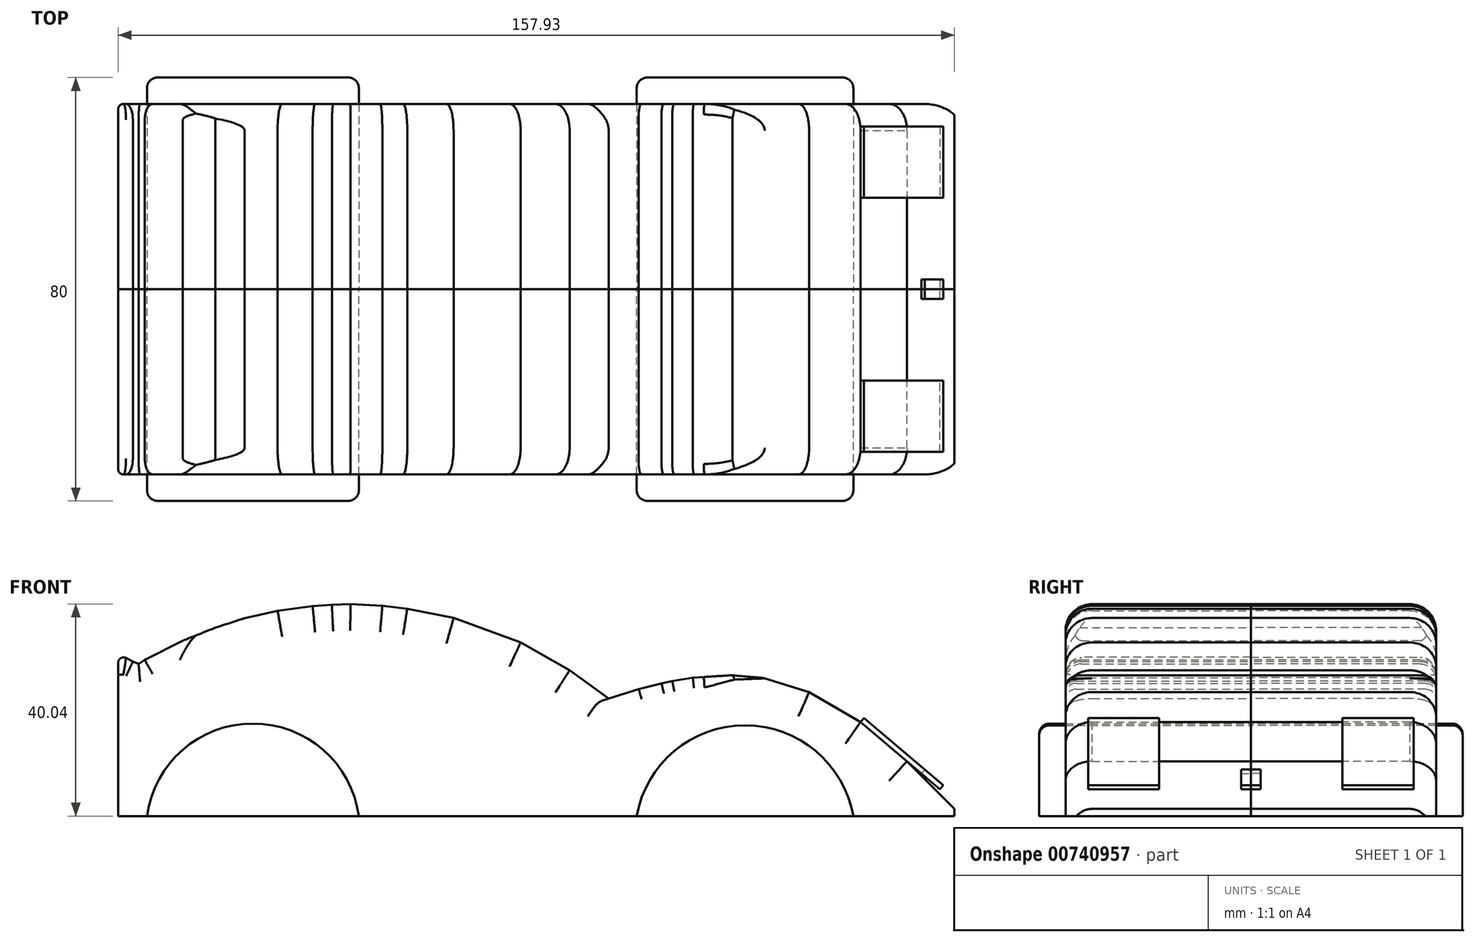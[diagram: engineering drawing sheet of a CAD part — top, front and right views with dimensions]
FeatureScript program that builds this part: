
annotation { "Feature Type Name" : "Feature", "Feature Type Description" : "" }
export const myFeature = defineFeature(function(context is Context, id is Id, definition is map)
    precondition{}
    {
        {
            var Q0;
            Q0=qCreatedBy(makeId("Front.planeOp"),FACE);
            var sketch = newSketch(context, id + "F0", { "sketchPlane" : qUnion([Q0])});
            skPoint(sketch, "E0.bottom.start.orphan", {"position": v(-35.35, 0) * mm});
            skLineSegment(sketch, "E1", {"start": v(-55.67, 30.52) * mm, "end": v(-53.12, 29.19) * mm});
            skPoint(sketch, "E2.startSnap0", {"position": v(70.97, 10.7) * mm});
            skPoint(sketch, "E3.orphan", {"position": v(70.97, 21.41) * mm});
            skPoint(sketch, "E4.orphan", {"position": v(-53.08, 6.08) * mm});
            skPoint(sketch, "E5.bottom.start.orphan", {"position": v(-55.9, 0) * mm});
            skPoint(sketch, "E6.orphan", {"position": v(-18.13, 0) * mm});
            skPoint(sketch, "E7.trimOffspring.end.orphan", {"position": v(70.97, 0) * mm});
            skPoint(sketch, "E8.orphan", {"position": v(86.43, 0) * mm});
            skPoint(sketch, "E9.orphan", {"position": v(86.43, 0.74) * mm});
            skPoint(sketch, "E10.0.internal.orphan", {"position": v(86.43, 10.7) * mm});
            skPoint(sketch, "E10.1.internal.orphan", {"position": v(102.02, 1.35) * mm});
            skLineSegment(sketch, "E11", {"start": v(102.02, 0) * mm, "end": v(102.02, 1.35) * mm});
            skLineSegment(sketch, "E12", {"start": v(102.02, 0) * mm, "end": v(-55.9, 0) * mm});
            skPoint(sketch, "E13.trimOffspring.end.orphan", {"position": v(-18.13, 6.08) * mm});
            skPoint(sketch, "E14.orphan", {"position": v(-18.13, 1.35) * mm});
            skPoint(sketch, "E15.start.orphan", {"position": v(86.43, 1.35) * mm});
            skArc(sketch, "E16", {"start": v(-10.44, 0) * mm, "mid": v(-30.45, 17.47) * mm, "end": v(-50.46, 0) * mm});
            skArc(sketch, "E17", {"start": v(82.95, 0) * mm, "mid": v(62.5, 17.15) * mm, "end": v(42.03, 0) * mm});
            skLineSegment(sketch, "E18", {"start": v(-55.88, 30.45) * mm, "end": v(-55.88, 30.6) * mm});
            skLineSegment(sketch, "E19", {"start": v(-55.88, 30.6) * mm, "end": v(-55.87, 30.6) * mm});
            skLineSegment(sketch, "E20", {"start": v(-55.87, 30.6) * mm, "end": v(-55.87, 30.6) * mm});
            skLineSegment(sketch, "E21", {"start": v(-55.87, 30.6) * mm, "end": v(-55.83, 30.58) * mm});
            skLineSegment(sketch, "E22", {"start": v(-55.83, 30.58) * mm, "end": v(-55.67, 30.52) * mm});
            skLineSegment(sketch, "E23", {"start": v(-53.12, 29.19) * mm, "end": v(-52.04, 28.74) * mm});
            skLineSegment(sketch, "E24", {"start": v(-52.04, 28.74) * mm, "end": v(-50.87, 29.48) * mm});
            skLineSegment(sketch, "E25", {"start": v(-50.87, 29.48) * mm, "end": v(-43.68, 33.14) * mm});
            skLineSegment(sketch, "E26", {"start": v(-43.68, 33.14) * mm, "end": v(-37.53, 35.58) * mm});
            skLineSegment(sketch, "E27", {"start": v(-37.53, 35.58) * mm, "end": v(-32, 37.39) * mm});
            skLineSegment(sketch, "E28", {"start": v(-32, 37.39) * mm, "end": v(-25.8, 38.8) * mm});
            skLineSegment(sketch, "E29", {"start": v(-25.8, 38.8) * mm, "end": v(-19.17, 39.68) * mm});
            skLineSegment(sketch, "E30", {"start": v(-19.17, 39.68) * mm, "end": v(-15.54, 39.9) * mm});
            skLineSegment(sketch, "E31", {"start": v(-15.54, 39.9) * mm, "end": v(-12.03, 40.04) * mm});
            skLineSegment(sketch, "E32", {"start": v(-12.03, 40.04) * mm, "end": v(-6, 39.73) * mm});
            skLineSegment(sketch, "E33", {"start": v(-6, 39.73) * mm, "end": v(-1.3, 39.18) * mm});
            skLineSegment(sketch, "E34", {"start": v(-1.3, 39.18) * mm, "end": v(7.45, 37.41) * mm});
            skLineSegment(sketch, "E35", {"start": v(7.45, 37.41) * mm, "end": v(20.12, 32.8) * mm});
            skLineSegment(sketch, "E36", {"start": v(20.12, 32.8) * mm, "end": v(29.37, 27.54) * mm});
            skLineSegment(sketch, "E37", {"start": v(29.37, 27.54) * mm, "end": v(36.73, 22.2) * mm});
            skLineSegment(sketch, "E38", {"start": v(36.73, 22.2) * mm, "end": v(42.42, 23.98) * mm});
            skLineSegment(sketch, "E39", {"start": v(42.42, 23.98) * mm, "end": v(46.72, 25.08) * mm});
            skLineSegment(sketch, "E40", {"start": v(46.72, 25.08) * mm, "end": v(48.75, 25.52) * mm});
            skLineSegment(sketch, "E41", {"start": v(48.75, 25.52) * mm, "end": v(52.63, 26.16) * mm});
            skLineSegment(sketch, "E42", {"start": v(52.63, 26.16) * mm, "end": v(60.13, 26.6) * mm});
            skLineSegment(sketch, "E43", {"start": v(60.13, 26.6) * mm, "end": v(66.02, 26.07) * mm});
            skLineSegment(sketch, "E44", {"start": v(66.02, 26.07) * mm, "end": v(74.6, 23.42) * mm});
            skLineSegment(sketch, "E45", {"start": v(74.6, 23.42) * mm, "end": v(84.32, 17.76) * mm});
            skLineSegment(sketch, "E46", {"start": v(84.32, 17.76) * mm, "end": v(93.1, 10.34) * mm});
            skLineSegment(sketch, "E47", {"start": v(93.1, 10.34) * mm, "end": v(102.02, 1.35) * mm});
            skPoint(sketch, "E48.end.orphan", {"position": v(-55.88, 1.35) * mm});
            skLineSegment(sketch, "E49", {"start": v(-55.88, 30.45) * mm, "end": v(-55.9, 0) * mm});
            skPoint(sketch, "E50.orphan", {"position": v(-12.61, 26.03) * mm});
            skPoint(sketch, "E51.start.orphan", {"position": v(-1.5, 24.26) * mm});
            skPoint(sketch, "E52.start.orphan", {"position": v(9.6, 22.5) * mm});
            skPoint(sketch, "E53.orphan", {"position": v(-6.97, 16.11) * mm});
            skPoint(sketch, "E54.start.orphan", {"position": v(-2.34, 16.11) * mm});
            skPoint(sketch, "E55.bottom.start.orphan", {"position": v(2.03, 16.11) * mm});
            skPoint(sketch, "E56.start.orphan", {"position": v(0, 16.11) * mm});
            skPoint(sketch, "E57.start.orphan", {"position": v(6.56, 6.08) * mm});
            skPoint(sketch, "E58.orphan", {"position": v(26.8, 6.08) * mm});
            skPoint(sketch, "E55.top.start.orphan", {"position": v(20.5, 6.08) * mm});
            skPoint(sketch, "E59.start.orphan", {"position": v(12.95, 16.11) * mm});
            skPoint(sketch, "E60.start.orphan", {"position": v(24.87, 16.11) * mm});
            skSolve(sketch);
        }
        {
            var Q0;
            {var subQ0=sQuery(id+"F0.wireOp",EDGE,"E16");Q0=makeQuery(id+"F0.imprint","IMPRINT",FACE,{"disambiguationData":[TD([[makeQuery(id+"F0.imprint","IMPRINT",EDGE,{"derivedFrom":subQ0}),1.0]])]});}
            var Q1;
            {var subQ0=sQuery(id+"F0.wireOp",EDGE,"E17");Q1=makeQuery(id+"F0.imprint","IMPRINT",FACE,{"disambiguationData":[TD([[makeQuery(id+"F0.imprint","IMPRINT",EDGE,{"derivedFrom":subQ0}),1.0]])]});}
            extrude(context, id + "F1", {"entities" : qUnion([Q0, Q1]), "depth" : 40 * mm, "offsetDistance" : 25 * mm});
        }
        {
            var Q0;
            {var subQ0=sQuery(id+"F0.wireOp",EDGE,"E16");Q0=makeQuery(id+"F0.imprint","IMPRINT",FACE,{"disambiguationData":[TD([[makeQuery(id+"F0.imprint","IMPRINT",EDGE,{"derivedFrom":subQ0}),-1.0]])]});}
            var Q1;
            {var subQ0=sQuery(id+"F0.wireOp",EDGE,"E17");Q1=makeQuery(id+"F0.imprint","IMPRINT",FACE,{"disambiguationData":[TD([[makeQuery(id+"F0.imprint","IMPRINT",EDGE,{"derivedFrom":subQ0}),-1.0]])]});}
            extrude(context, id + "F2", {"entities" : qUnion([Q0, Q1]), "depth" : 35 * mm, "offsetDistance" : 25 * mm});
        }
        {
            var Q0;
            Q0=makeQuery(id+"F1.opExtrude","CAP_EDGE",EDGE,{"disambiguationData":[OSD([sQuery(id+"F0.wireOp",EDGE,"E17")])],"isStart":false});
            var Q1;
            Q1=makeQuery(id+"F1.opExtrude","CAP_EDGE",EDGE,{"disambiguationData":[OSD([sQuery(id+"F0.wireOp",EDGE,"E16")])],"isStart":false});
            fillet(context, id + "F3", {"entities" : qUnion([Q0, Q1]), "radius" : 2 * mm, "tangentPropagation" : true, "allowEdgeOverflow" : false});
        }
        {
            var Q0;
            {var subQ0=sQuery(id+"F0.wireOp",EDGE,"E29");Q0=makeQuery(id+"Fo0DXlsXbwqjUcK_2.opFillet","BLEND_EDGE",EDGE,{"blendedFrom":[makeQuery(id+"F2.opExtrude","CAP_EDGE",EDGE,{"disambiguationData":[OSD([subQ0])],"isStart":false}),makeQuery(id+"F2.opExtrude","SWEPT_FACE",FACE,{"disambiguationData":[OSD([subQ0])]})],"blendedInto":[makeQuery(id+"F2.opExtrude","SWEPT_FACE",FACE,{"disambiguationData":[OSD([subQ0])]})]});}
            var Q1;
            Q1=makeQuery(id+"Fo0DXlsXbwqjUcK_2.opFillet","BLEND_EDGE",EDGE,{"blendedFrom":[makeQuery(id+"F2.opExtrude","CAP_EDGE",EDGE,{"disambiguationData":[OSD([sQuery(id+"F0.wireOp",EDGE,"E29")])],"isStart":false}),makeQuery(id+"F2.opExtrude","SWEPT_FACE",FACE,{"disambiguationData":[OSD([sQuery(id+"F0.wireOp",EDGE,"E28")])]})],"blendedInto":[makeQuery(id+"F2.opExtrude","SWEPT_FACE",FACE,{"disambiguationData":[OSD([sQuery(id+"F0.wireOp",EDGE,"E28")])]})]});
            var Q2;
            Q2=makeQuery(id+"Fo0DXlsXbwqjUcK_2.opFillet","BLEND_EDGE",EDGE,{"blendedFrom":[makeQuery(id+"F2.opExtrude","CAP_EDGE",EDGE,{"disambiguationData":[OSD([sQuery(id+"F0.wireOp",EDGE,"E29")])],"isStart":false}),makeQuery(id+"F2.opExtrude","SWEPT_FACE",FACE,{"disambiguationData":[OSD([sQuery(id+"F0.wireOp",EDGE,"E27")])]})],"blendedInto":[makeQuery(id+"F2.opExtrude","SWEPT_FACE",FACE,{"disambiguationData":[OSD([sQuery(id+"F0.wireOp",EDGE,"E27")])]})]});
            var Q3;
            Q3=makeQuery(id+"Fo0DXlsXbwqjUcK_2.opFillet","BLEND_EDGE",EDGE,{"blendedFrom":[makeQuery(id+"F2.opExtrude","CAP_EDGE",EDGE,{"disambiguationData":[OSD([sQuery(id+"F0.wireOp",EDGE,"E29")])],"isStart":false}),makeQuery(id+"F2.opExtrude","SWEPT_FACE",FACE,{"disambiguationData":[OSD([sQuery(id+"F0.wireOp",EDGE,"E26")])]})],"blendedInto":[makeQuery(id+"F2.opExtrude","SWEPT_FACE",FACE,{"disambiguationData":[OSD([sQuery(id+"F0.wireOp",EDGE,"E26")])]})]});
            var Q4;
            Q4=makeQuery(id+"Fo0DXlsXbwqjUcK_2.opFillet","BLEND_EDGE",EDGE,{"blendedFrom":[makeQuery(id+"F2.opExtrude","CAP_EDGE",EDGE,{"disambiguationData":[OSD([sQuery(id+"F0.wireOp",EDGE,"E29")])],"isStart":false}),makeQuery(id+"F2.opExtrude","SWEPT_FACE",FACE,{"disambiguationData":[OSD([sQuery(id+"F0.wireOp",EDGE,"E25")])]})],"blendedInto":[makeQuery(id+"F2.opExtrude","SWEPT_FACE",FACE,{"disambiguationData":[OSD([sQuery(id+"F0.wireOp",EDGE,"E25")])]})]});
            var Q5;
            Q5=makeQuery(id+"F2.opExtrude","CAP_EDGE",EDGE,{"disambiguationData":[OSD([sQuery(id+"F0.wireOp",EDGE,"E24")])],"isStart":false});
            var Q6;
            Q6=makeQuery(id+"F2.opExtrude","CAP_EDGE",EDGE,{"disambiguationData":[OSD([sQuery(id+"F0.wireOp",EDGE,"E23")])],"isStart":false});
            var Q7;
            Q7=makeQuery(id+"F2.opExtrude","CAP_EDGE",EDGE,{"disambiguationData":[OSD([sQuery(id+"F0.wireOp",EDGE,"E25")])],"isStart":false});
            var Q8;
            Q8=makeQuery(id+"F2.opExtrude","CAP_EDGE",EDGE,{"disambiguationData":[OSD([sQuery(id+"F0.wireOp",EDGE,"E1")])],"isStart":false});
            fillet(context, id + "F4", {"entities" : qUnion([Q0, Q1, Q2, Q3, Q4, Q5, Q6, Q7, Q8]), "radius" : 3 * mm, "tangentPropagation" : true, "allowEdgeOverflow" : false});
        }
        {
            var Q0;
            Q0=makeQuery(id+"F2.opExtrude","CAP_EDGE",EDGE,{"disambiguationData":[OSD([sQuery(id+"F0.wireOp",EDGE,"E47")])],"isStart":false});
            var Q1;
            Q1=makeQuery(id+"F2.opExtrude","CAP_EDGE",EDGE,{"disambiguationData":[OSD([sQuery(id+"F0.wireOp",EDGE,"E46")])],"isStart":false});
            var Q2;
            Q2=makeQuery(id+"F2.opExtrude","CAP_EDGE",EDGE,{"disambiguationData":[OSD([sQuery(id+"F0.wireOp",EDGE,"E45")])],"isStart":false});
            var Q3;
            Q3=makeQuery(id+"F2.opExtrude","CAP_EDGE",EDGE,{"disambiguationData":[OSD([sQuery(id+"F0.wireOp",EDGE,"E44")])],"isStart":false});
            fillet(context, id + "F5", {"entities" : qUnion([Q0, Q1, Q2, Q3]), "radius" : 5 * mm, "tangentPropagation" : true, "allowEdgeOverflow" : false});
        }
        {
            var Q0;
            Q0=makeQuery(id+"F5.opFillet","BLEND_EDGE",EDGE,{"blendedFrom":[makeQuery(id+"F2.opExtrude","CAP_EDGE",EDGE,{"disambiguationData":[OSD([sQuery(id+"F0.wireOp",EDGE,"E44")])],"isStart":false}),makeQuery(id+"F2.opExtrude","SWEPT_FACE",FACE,{"disambiguationData":[OSD([sQuery(id+"F0.wireOp",EDGE,"E41")])]})],"blendedInto":[makeQuery(id+"F2.opExtrude","SWEPT_FACE",FACE,{"disambiguationData":[OSD([sQuery(id+"F0.wireOp",EDGE,"E41")])]})]});
            var Q1;
            Q1=makeQuery(id+"F5.opFillet","BLEND_EDGE",EDGE,{"blendedFrom":[makeQuery(id+"F2.opExtrude","CAP_EDGE",EDGE,{"disambiguationData":[OSD([sQuery(id+"F0.wireOp",EDGE,"E44")])],"isStart":false}),makeQuery(id+"F2.opExtrude","SWEPT_FACE",FACE,{"disambiguationData":[OSD([sQuery(id+"F0.wireOp",EDGE,"E42")])]})],"blendedInto":[makeQuery(id+"F2.opExtrude","SWEPT_FACE",FACE,{"disambiguationData":[OSD([sQuery(id+"F0.wireOp",EDGE,"E42")])]})]});
            var Q2;
            Q2=makeQuery(id+"F5.opFillet","BLEND_EDGE",EDGE,{"blendedFrom":[makeQuery(id+"F2.opExtrude","CAP_EDGE",EDGE,{"disambiguationData":[OSD([sQuery(id+"F0.wireOp",EDGE,"E44")])],"isStart":false}),makeQuery(id+"F2.opExtrude","SWEPT_FACE",FACE,{"disambiguationData":[OSD([sQuery(id+"F0.wireOp",EDGE,"E43")])]})],"blendedInto":[makeQuery(id+"F2.opExtrude","SWEPT_FACE",FACE,{"disambiguationData":[OSD([sQuery(id+"F0.wireOp",EDGE,"E43")])]})]});
            var Q3;
            Q3=makeQuery(id+"F2.opExtrude","CAP_EDGE",EDGE,{"disambiguationData":[OSD([sQuery(id+"F0.wireOp",EDGE,"E38")])],"isStart":false});
            var Q4;
            Q4=makeQuery(id+"F2.opExtrude","CAP_EDGE",EDGE,{"disambiguationData":[OSD([sQuery(id+"F0.wireOp",EDGE,"E39")])],"isStart":false});
            var Q5;
            Q5=makeQuery(id+"F2.opExtrude","CAP_EDGE",EDGE,{"disambiguationData":[OSD([sQuery(id+"F0.wireOp",EDGE,"E40")])],"isStart":false});
            var Q6;
            Q6=makeQuery(id+"F2.opExtrude","CAP_EDGE",EDGE,{"disambiguationData":[OSD([sQuery(id+"F0.wireOp",EDGE,"E41")])],"isStart":false});
            fillet(context, id + "F6", {"entities" : qUnion([Q0, Q1, Q2, Q3, Q4, Q5, Q6]), "radius" : 2 * mm, "tangentPropagation" : true, "allowEdgeOverflow" : false});
        }
        {
            var Q0;
            Q0=makeQuery(id+"F2.opExtrude","CAP_EDGE",EDGE,{"disambiguationData":[OSD([sQuery(id+"F0.wireOp",EDGE,"E49")])],"isStart":false});
            fillet(context, id + "F7", {"entities" : qUnion([Q0]), "radius" : 1 * mm, "tangentPropagation" : true, "allowEdgeOverflow" : false});
        }
        {
            var Q0;
            Q0=makeQuery(id+"F2.opExtrude","CAP_EDGE",EDGE,{"disambiguationData":[OSD([sQuery(id+"F0.wireOp",EDGE,"E29")])],"isStart":false});
            var Q1;
            Q1=makeQuery(id+"F2.opExtrude","CAP_EDGE",EDGE,{"disambiguationData":[OSD([sQuery(id+"F0.wireOp",EDGE,"E32")])],"isStart":false});
            var Q2;
            Q2=makeQuery(id+"F2.opExtrude","CAP_EDGE",EDGE,{"disambiguationData":[OSD([sQuery(id+"F0.wireOp",EDGE,"E31")])],"isStart":false});
            var Q3;
            Q3=makeQuery(id+"F2.opExtrude","CAP_EDGE",EDGE,{"disambiguationData":[OSD([sQuery(id+"F0.wireOp",EDGE,"E30")])],"isStart":false});
            var Q4;
            Q4=makeQuery(id+"F2.opExtrude","CAP_EDGE",EDGE,{"disambiguationData":[OSD([sQuery(id+"F0.wireOp",EDGE,"E33")])],"isStart":false});
            var Q5;
            Q5=makeQuery(id+"F2.opExtrude","CAP_EDGE",EDGE,{"disambiguationData":[OSD([sQuery(id+"F0.wireOp",EDGE,"E34")])],"isStart":false});
            var Q6;
            Q6=makeQuery(id+"F2.opExtrude","CAP_EDGE",EDGE,{"disambiguationData":[OSD([sQuery(id+"F0.wireOp",EDGE,"E35")])],"isStart":false});
            var Q7;
            Q7=makeQuery(id+"F2.opExtrude","CAP_EDGE",EDGE,{"disambiguationData":[OSD([sQuery(id+"F0.wireOp",EDGE,"E36")])],"isStart":false});
            var Q8;
            Q8=makeQuery(id+"F2.opExtrude","CAP_EDGE",EDGE,{"disambiguationData":[OSD([sQuery(id+"F0.wireOp",EDGE,"E37")])],"isStart":false});
            var Q9;
            Q9=makeQuery(id+"F4.opFillet","BLEND_EDGE",EDGE,{"blendedFrom":[makeQuery(id+"F2.opExtrude","CAP_EDGE",EDGE,{"disambiguationData":[OSD([sQuery(id+"F0.wireOp",EDGE,"E25")])],"isStart":false}),makeQuery(id+"F2.opExtrude","SWEPT_FACE",FACE,{"disambiguationData":[OSD([sQuery(id+"F0.wireOp",EDGE,"E28")])]})],"blendedInto":[makeQuery(id+"F2.opExtrude","SWEPT_FACE",FACE,{"disambiguationData":[OSD([sQuery(id+"F0.wireOp",EDGE,"E28")])]})]});
            fillet(context, id + "F8", {"entities" : qUnion([Q0, Q1, Q2, Q3, Q4, Q5, Q6, Q7, Q8, Q9]), "radius" : 5 * mm, "tangentPropagation" : true, "allowEdgeOverflow" : false});
        }
        {
            var Q0;
            Q0=makeQuery(id+"F2.opExtrude","SWEPT_FACE",FACE,{"disambiguationData":[OSD([sQuery(id+"F0.wireOp",EDGE,"E46")])]});
            var sketch = newSketch(context, id + "F9", { "sketchPlane" : qUnion([Q0])});
            skLineSegment(sketch, "E61.bottom", {"start": v(52.9, -30.74) * mm, "end": v(72.54, -30.74) * mm});
            skLineSegment(sketch, "E61.top", {"start": v(52.9, -17.3) * mm, "end": v(72.54, -17.3) * mm});
            skLineSegment(sketch, "E61.left", {"start": v(52.9, -30.74) * mm, "end": v(52.9, -17.3) * mm});
            skLineSegment(sketch, "E61.right", {"start": v(72.54, -30.74) * mm, "end": v(72.54, -17.3) * mm});
            skPoint(sketch, "E62.firstSnap0", {"position": v(72.54, -24.02) * mm});
            skLineSegment(sketch, "E62.bottom", {"start": v(72.54, -1.84) * mm, "end": v(67.94, -1.84) * mm});
            skLineSegment(sketch, "E62.top", {"start": v(72.54, 0) * mm, "end": v(67.94, 0) * mm});
            skLineSegment(sketch, "E62.left", {"start": v(72.54, -1.84) * mm, "end": v(72.54, 0) * mm});
            skLineSegment(sketch, "E62.right", {"start": v(67.94, -1.84) * mm, "end": v(67.94, 0) * mm});
            skSolve(sketch);
        }
        {
            var Q0;
            {var subQ0=sQuery(id+"F9.wireOp",EDGE,"E61.left");Q0=makeQuery(id+"F9.imprint","IMPRINT",FACE,{"disambiguationData":[TD([[makeQuery(id+"F9.imprint","IMPRINT",EDGE,{"derivedFrom":subQ0}),-1.0]])]});}
            var Q1;
            {var subQ0=sQuery(id+"F9.wireOp",EDGE,"E61.right");Q1=makeQuery(id+"F9.imprint","IMPRINT",FACE,{"disambiguationData":[TD([[makeQuery(id+"F9.imprint","IMPRINT",EDGE,{"derivedFrom":subQ0}),1.0]])]});}
            extrude(context, id + "F10", {"entities" : qUnion([Q0, Q1]), "operationType" : NewBodyOperationType.ADD, "depth" : 1 * mm, "offsetDistance" : 25 * mm});
        }
        {
            var Q0;
            Q0=makeQuery(id+"F9.imprint","IMPRINT",FACE,{"disambiguationData":[TD([[makeQuery(id+"F9.imprint","IMPRINT",EDGE,{"derivedFrom":sQuery(id+"F9.wireOp",EDGE,"E62.bottom")}),-1.0]])]});
            extrude(context, id + "F11", {"entities" : qUnion([Q0]), "depth" : 1 * mm, "offsetDistance" : 25 * mm});
        }
        {
            var Q0;
            Q0=makeQuery(id+"F1.opExtrude","SWEPT_BODY",BODY,{"disambiguationData":[OSD([sQuery(id+"F0.wireOp",EDGE,"E12"),sQuery(id+"F0.wireOp",EDGE,"E16")])]});
            var Q1;
            Q1=makeQuery(id+"F1.opExtrude","SWEPT_BODY",BODY,{"disambiguationData":[OSD([sQuery(id+"F0.wireOp",EDGE,"E12"),sQuery(id+"F0.wireOp",EDGE,"E17")])]});
            var Q2;
            Q2=makeQuery(id+"F11.opExtrude","SWEPT_BODY",BODY,{"disambiguationData":[OSD([sQuery(id+"F9.wireOp",EDGE,"E62.bottom"),sQuery(id+"F9.wireOp",EDGE,"E62.top"),sQuery(id+"F9.wireOp",EDGE,"E62.left"),sQuery(id+"F9.wireOp",EDGE,"E62.right")])]});
            var Q3;
            Q3=makeQuery(id+"F2.opExtrude","SWEPT_BODY",BODY,{"disambiguationData":[OSD([sQuery(id+"F0.wireOp",EDGE,"E1"),sQuery(id+"F0.wireOp",EDGE,"E11"),sQuery(id+"F0.wireOp",EDGE,"E12"),sQuery(id+"F0.wireOp",EDGE,"E16"),sQuery(id+"F0.wireOp",EDGE,"E17"),sQuery(id+"F0.wireOp",EDGE,"E18"),sQuery(id+"F0.wireOp",EDGE,"E19"),sQuery(id+"F0.wireOp",EDGE,"E20"),sQuery(id+"F0.wireOp",EDGE,"E21"),sQuery(id+"F0.wireOp",EDGE,"E22"),sQuery(id+"F0.wireOp",EDGE,"E23"),sQuery(id+"F0.wireOp",EDGE,"E24"),sQuery(id+"F0.wireOp",EDGE,"E25"),sQuery(id+"F0.wireOp",EDGE,"E26"),sQuery(id+"F0.wireOp",EDGE,"E27"),sQuery(id+"F0.wireOp",EDGE,"E28"),sQuery(id+"F0.wireOp",EDGE,"E29"),sQuery(id+"F0.wireOp",EDGE,"E30"),sQuery(id+"F0.wireOp",EDGE,"E31"),sQuery(id+"F0.wireOp",EDGE,"E32"),sQuery(id+"F0.wireOp",EDGE,"E33"),sQuery(id+"F0.wireOp",EDGE,"E34"),sQuery(id+"F0.wireOp",EDGE,"E35"),sQuery(id+"F0.wireOp",EDGE,"E36"),sQuery(id+"F0.wireOp",EDGE,"E37"),sQuery(id+"F0.wireOp",EDGE,"E38"),sQuery(id+"F0.wireOp",EDGE,"E39"),sQuery(id+"F0.wireOp",EDGE,"E40"),sQuery(id+"F0.wireOp",EDGE,"E41"),sQuery(id+"F0.wireOp",EDGE,"E42"),sQuery(id+"F0.wireOp",EDGE,"E43"),sQuery(id+"F0.wireOp",EDGE,"E44"),sQuery(id+"F0.wireOp",EDGE,"E45"),sQuery(id+"F0.wireOp",EDGE,"E46"),sQuery(id+"F0.wireOp",EDGE,"E47"),sQuery(id+"F0.wireOp",EDGE,"E49")])]});
            var Q4;
            Q4=qCreatedBy(makeId("Front.planeOp"),FACE);
            mirror(context, id + "F12", {"entities" : qUnion([Q0, Q1, Q2, Q3]), "mirrorPlane" : qUnion([Q4])});
        }
    });
